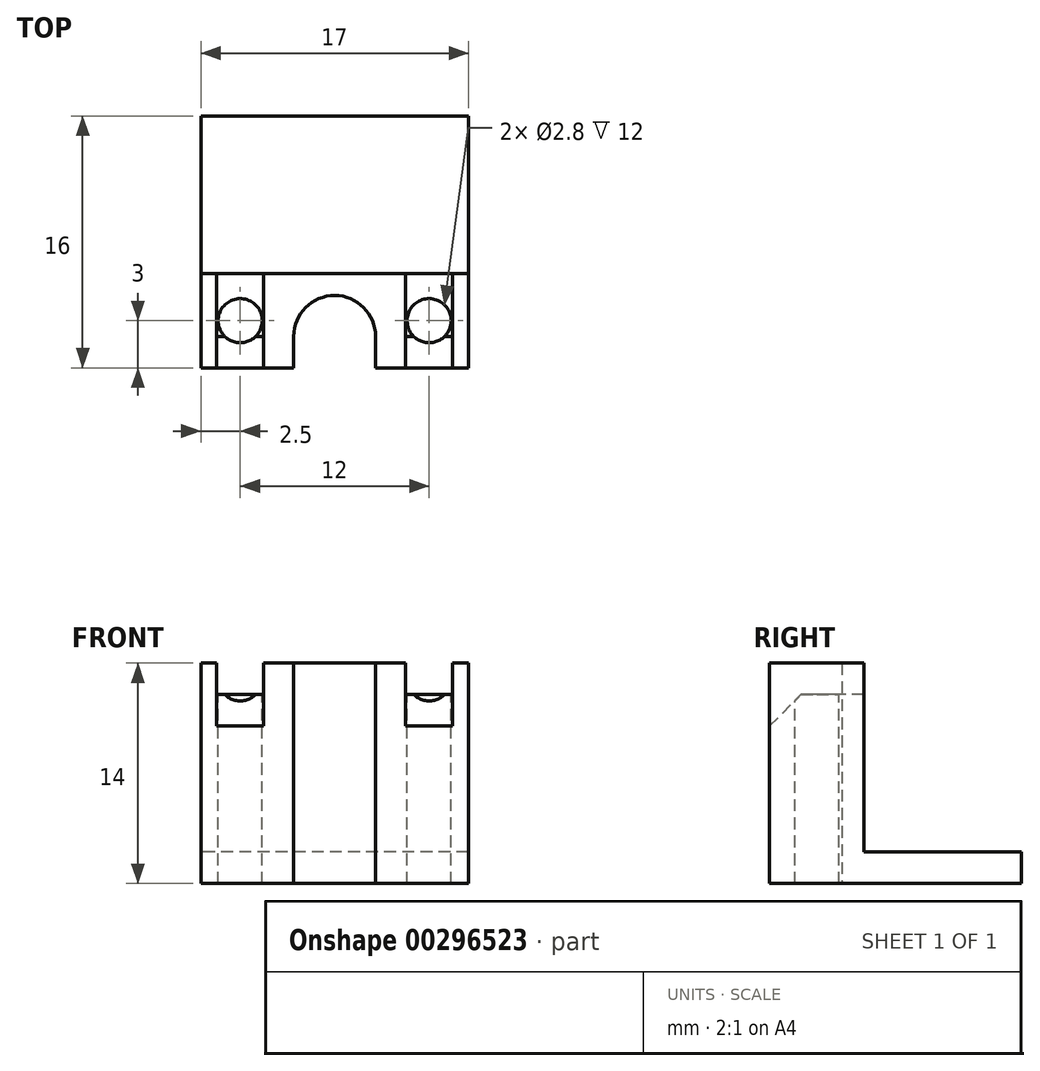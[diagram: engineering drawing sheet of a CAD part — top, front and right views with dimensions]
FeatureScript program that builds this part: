
annotation { "Feature Type Name" : "Feature", "Feature Type Description" : "" }
export const myFeature = defineFeature(function(context is Context, id is Id, definition is map)
    precondition{}
    {
        {
            var Q0;
            Q0=qCreatedBy(makeId("Top.planeOp"),FACE);
            var sketch = newSketch(context, id + "F0", { "sketchPlane" : qUnion([Q0])});
            skLineSegment(sketch, "E0", {"start": v(0, 0) * mm, "end": v(5.9, 0) * mm});
            skLineSegment(sketch, "E1", {"start": v(5.9, 0) * mm, "end": v(5.9, 6) * mm});
            skLineSegment(sketch, "E2", {"start": v(5.9, 6) * mm, "end": v(-2.6, 6) * mm});
            skLineSegment(sketch, "E3", {"start": v(-2.6, 6) * mm, "end": v(-2.6, 4.6) * mm});
            skLineSegment(sketch, "E4", {"start": v(0, 0) * mm, "end": v(0, 2) * mm});
            skArc(sketch, "E5", {"start": v(0, 2) * mm, "mid": v(-0.76, 3.84) * mm, "end": v(-2.6, 4.6) * mm});
            skPoint(sketch, "E6.positionSnap0", {"position": v(5.9, 3) * mm});
            skLineSegment(sketch, "E7", {"start": v(5.9, 6) * mm, "end": v(5.9, 16) * mm});
            skLineSegment(sketch, "E8", {"start": v(5.9, 16) * mm, "end": v(-2.6, 16) * mm});
            skLineSegment(sketch, "E9", {"start": v(-2.6, 16) * mm, "end": v(-2.6, 6) * mm});
            skSolve(sketch);
        }
        {
            var Q0;
            Q0=makeQuery(id+"F0.imprint","IMPRINT",FACE,{"disambiguationData":[TD([[makeQuery(id+"F0.imprint","IMPRINT",EDGE,{"derivedFrom":sQuery(id+"F0.wireOp",EDGE,"E0")}),1.0]])]});
            extrude(context, id + "F1", {"entities" : qUnion([Q0]), "depth" : 12 * mm});
        }
        {
            var Q0;
            Q0=makeQuery(id+"F0.imprint","IMPRINT",FACE,{"disambiguationData":[TD([[makeQuery(id+"F0.imprint","IMPRINT",EDGE,{"derivedFrom":sQuery(id+"F0.wireOp",EDGE,"E2")}),-1.0]])]});
            extrude(context, id + "F2", {"entities" : qUnion([Q0]), "operationType" : NewBodyOperationType.ADD, "depth" : 2 * mm});
        }
        {
            var Q0;
            Q0=makeQuery(id+"F1.opExtrude","CAP_FACE",FACE,{"disambiguationData":[OSD([sQuery(id+"F0.wireOp",EDGE,"E0"),sQuery(id+"F0.wireOp",EDGE,"E1"),sQuery(id+"F0.wireOp",EDGE,"E2"),sQuery(id+"F0.wireOp",EDGE,"E3"),sQuery(id+"F0.wireOp",EDGE,"E4"),sQuery(id+"F0.wireOp",EDGE,"E5")])],"isStart":false});
            var sketch = newSketch(context, id + "F3", { "sketchPlane" : qUnion([Q0])});
            skPoint(sketch, "E10", {"position": v(3.4, 3) * mm});
            skPoint(sketch, "E10.positionSnap0", {"position": v(5.9, 3) * mm});
            skSolve(sketch);
        }
        {
            var Q0;
            Q0=sQuery(id+"F3.wireOp",VERTEX,"E10");
            var Q1;
            Q1=makeQuery(id+"F1.opExtrude","SWEPT_BODY",BODY,{"disambiguationData":[OSD([sQuery(id+"F0.wireOp",EDGE,"E0"),sQuery(id+"F0.wireOp",EDGE,"E1"),sQuery(id+"F0.wireOp",EDGE,"E2"),sQuery(id+"F0.wireOp",EDGE,"E3"),sQuery(id+"F0.wireOp",EDGE,"E4"),sQuery(id+"F0.wireOp",EDGE,"E5")])]});
            hole(context, id + "F4", {"style" : HoleStyle.SIMPLE, "endStyle" : HoleEndStyle.THROUGH, "holeDiameter" : 2.8 * mm, "tappedDepth" : 12 * mm, "tapClearance" : 3, "locations" : qUnion([Q0]), "scope" : qUnion([Q1])});
        }
        {
            var Q0;
            Q0=makeQuery(id+"F1.opExtrude","SWEPT_BODY",BODY,{"disambiguationData":[OSD([sQuery(id+"F0.wireOp",EDGE,"E0"),sQuery(id+"F0.wireOp",EDGE,"E1"),sQuery(id+"F0.wireOp",EDGE,"E2"),sQuery(id+"F0.wireOp",EDGE,"E3"),sQuery(id+"F0.wireOp",EDGE,"E4"),sQuery(id+"F0.wireOp",EDGE,"E5")])]});
            var Q1;
            Q1=makeQuery(id+"F1.opExtrude","SWEPT_FACE",FACE,{"disambiguationData":[OSD([sQuery(id+"F0.wireOp",EDGE,"E3")])]});
            mirror(context, id + "F5", {"operationType" : NewBodyOperationType.ADD, "entities" : qUnion([Q0]), "mirrorPlane" : qUnion([Q1])});
        }
        {
            var Q0;
            {var subQ0=makeQuery(id+"F1.opExtrude","CAP_FACE",FACE,{"disambiguationData":[OSD([sQuery(id+"F0.wireOp",EDGE,"E0"),sQuery(id+"F0.wireOp",EDGE,"E1"),sQuery(id+"F0.wireOp",EDGE,"E2"),sQuery(id+"F0.wireOp",EDGE,"E3"),sQuery(id+"F0.wireOp",EDGE,"E4"),sQuery(id+"F0.wireOp",EDGE,"E5")])],"isStart":false});Q0=makeQuery(id+"F5.boolean.opBoolean","MERGE",FACE,{"derivedFrom":[subQ0,makeQuery(id+"F5.opPattern","COPY",FACE,{"derivedFrom":subQ0,"instanceName":"1"})]});}
            var sketch = newSketch(context, id + "F6", { "sketchPlane" : qUnion([Q0])});
            skLineSegment(sketch, "E11", {"start": v(-10.1, 6) * mm, "end": v(-10.1, 0) * mm});
            skLineSegment(sketch, "E12", {"start": v(-7.1, 6) * mm, "end": v(-7.1, 0) * mm});
            skLineSegment(sketch, "E13", {"start": v(4.9, 6) * mm, "end": v(4.9, 0) * mm});
            skLineSegment(sketch, "E14", {"start": v(1.9, 6) * mm, "end": v(1.9, 0) * mm});
            skSolve(sketch);
        }
        {
            var Q0;
            {var subQ0=sQuery(id+"F6.wireOp",EDGE,"E11");Q0=makeQuery(id+"F6.imprint","IMPRINT",FACE,{"disambiguationData":[TD([[makeQuery(id+"F6.imprint","IMPRINT",EDGE,{"derivedFrom":subQ0}),-1.0]])]});}
            var Q1;
            {var subQ5=sQuery(id+"F6.wireOp",EDGE,"E12");Q1=makeQuery(id+"F6.imprint","IMPRINT",FACE,{"disambiguationData":[TD([[makeQuery(id+"F6.imprint","IMPRINT",EDGE,{"derivedFrom":subQ5}),1.0]])]});}
            var Q2;
            {var subQ0=sQuery(id+"F6.wireOp",EDGE,"E13");Q2=makeQuery(id+"F6.imprint","IMPRINT",FACE,{"disambiguationData":[TD([[makeQuery(id+"F6.imprint","IMPRINT",EDGE,{"derivedFrom":subQ0}),1.0]])]});}
            extrude(context, id + "F7", {"entities" : qUnion([Q0, Q1, Q2]), "operationType" : NewBodyOperationType.ADD, "depth" : 2 * mm});
        }
        {
            var Q0;
            Q0=makeQuery(id+"F5.opPattern","COPY",EDGE,{"derivedFrom":makeQuery(id+"F1.opExtrude","CAP_EDGE",EDGE,{"disambiguationData":[OSD([sQuery(id+"F0.wireOp",EDGE,"E0")])],"isStart":false}),"instanceName":"1"});
            var Q1;
            Q1=makeQuery(id+"F1.opExtrude","CAP_EDGE",EDGE,{"disambiguationData":[OSD([sQuery(id+"F0.wireOp",EDGE,"E0")])],"isStart":false});
            chamfer(context, id + "F8", {"entities" : qUnion([Q0, Q1]), "width" : 2 * mm, "tangentPropagation" : true});
        }
    });
